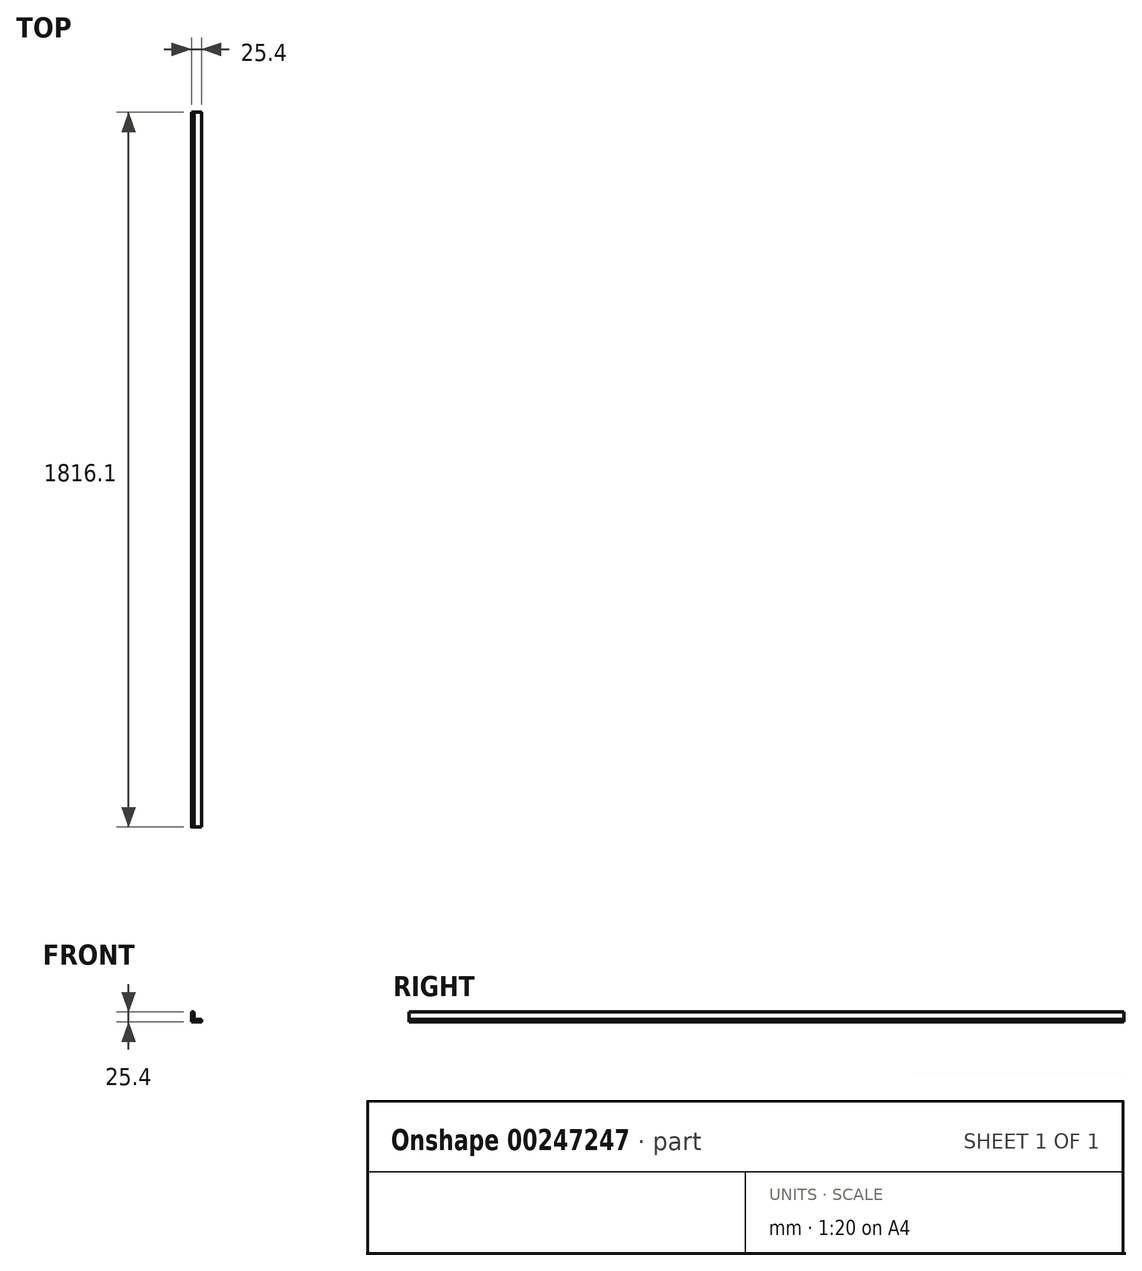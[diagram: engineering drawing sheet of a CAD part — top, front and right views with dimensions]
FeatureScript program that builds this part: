
annotation { "Feature Type Name" : "Feature", "Feature Type Description" : "" }
export const myFeature = defineFeature(function(context is Context, id is Id, definition is map)
    precondition{}
    {
        {
            var Q0;
            Q0=qCreatedBy(makeId("Front.planeOp"),FACE);
            var sketch = newSketch(context, id + "F0", { "sketchPlane" : qUnion([Q0])});
            skLineSegment(sketch, "E0", {"start": v(0, 0) * mm, "end": v(23.88, 0) * mm});
            skLineSegment(sketch, "E1", {"start": v(25.4, 1.52) * mm, "end": v(25.4, 4.83) * mm});
            skLineSegment(sketch, "E2", {"start": v(23.88, 6.35) * mm, "end": v(7.87, 6.35) * mm});
            skLineSegment(sketch, "E3", {"start": v(6.35, 7.87) * mm, "end": v(6.35, 23.88) * mm});
            skLineSegment(sketch, "E4", {"start": v(4.83, 25.4) * mm, "end": v(1.52, 25.4) * mm});
            skLineSegment(sketch, "E5", {"start": v(0, 23.88) * mm, "end": v(0, 0) * mm});
            skPoint(sketch, "E6.visualSharp", {"position": v(0, 25.4) * mm});
            skArc(sketch, "E6.filletArc", {"start": v(1.52, 25.4) * mm, "mid": v(0.45, 24.95) * mm, "end": v(0, 23.88) * mm});
            skPoint(sketch, "E7.visualSharp", {"position": v(6.35, 25.4) * mm});
            skArc(sketch, "E7.filletArc", {"start": v(6.35, 23.88) * mm, "mid": v(5.9, 24.95) * mm, "end": v(4.83, 25.4) * mm});
            skPoint(sketch, "E8.visualSharp", {"position": v(6.35, 6.35) * mm});
            skArc(sketch, "E8.filletArc", {"start": v(6.35, 7.87) * mm, "mid": v(6.8, 6.8) * mm, "end": v(7.87, 6.35) * mm});
            skPoint(sketch, "E9.visualSharp", {"position": v(25.4, 6.35) * mm});
            skArc(sketch, "E9.filletArc", {"start": v(25.4, 4.83) * mm, "mid": v(24.95, 5.9) * mm, "end": v(23.88, 6.35) * mm});
            skPoint(sketch, "E10.visualSharp", {"position": v(25.4, 0) * mm});
            skArc(sketch, "E10.filletArc", {"start": v(23.88, 0) * mm, "mid": v(24.95, 0.45) * mm, "end": v(25.4, 1.52) * mm});
            skSolve(sketch);
        }
        {
            var Q0;
            Q0=makeQuery(id+"F0.imprint","IMPRINT",FACE,{"disambiguationData":[TD([[makeQuery(id+"F0.imprint","IMPRINT",EDGE,{"derivedFrom":sQuery(id+"F0.wireOp",EDGE,"E0")}),1.0]])]});
            extrude(context, id + "F1", {"entities" : qUnion([Q0]), "depth" : 1816.1 * mm});
        }
    });
